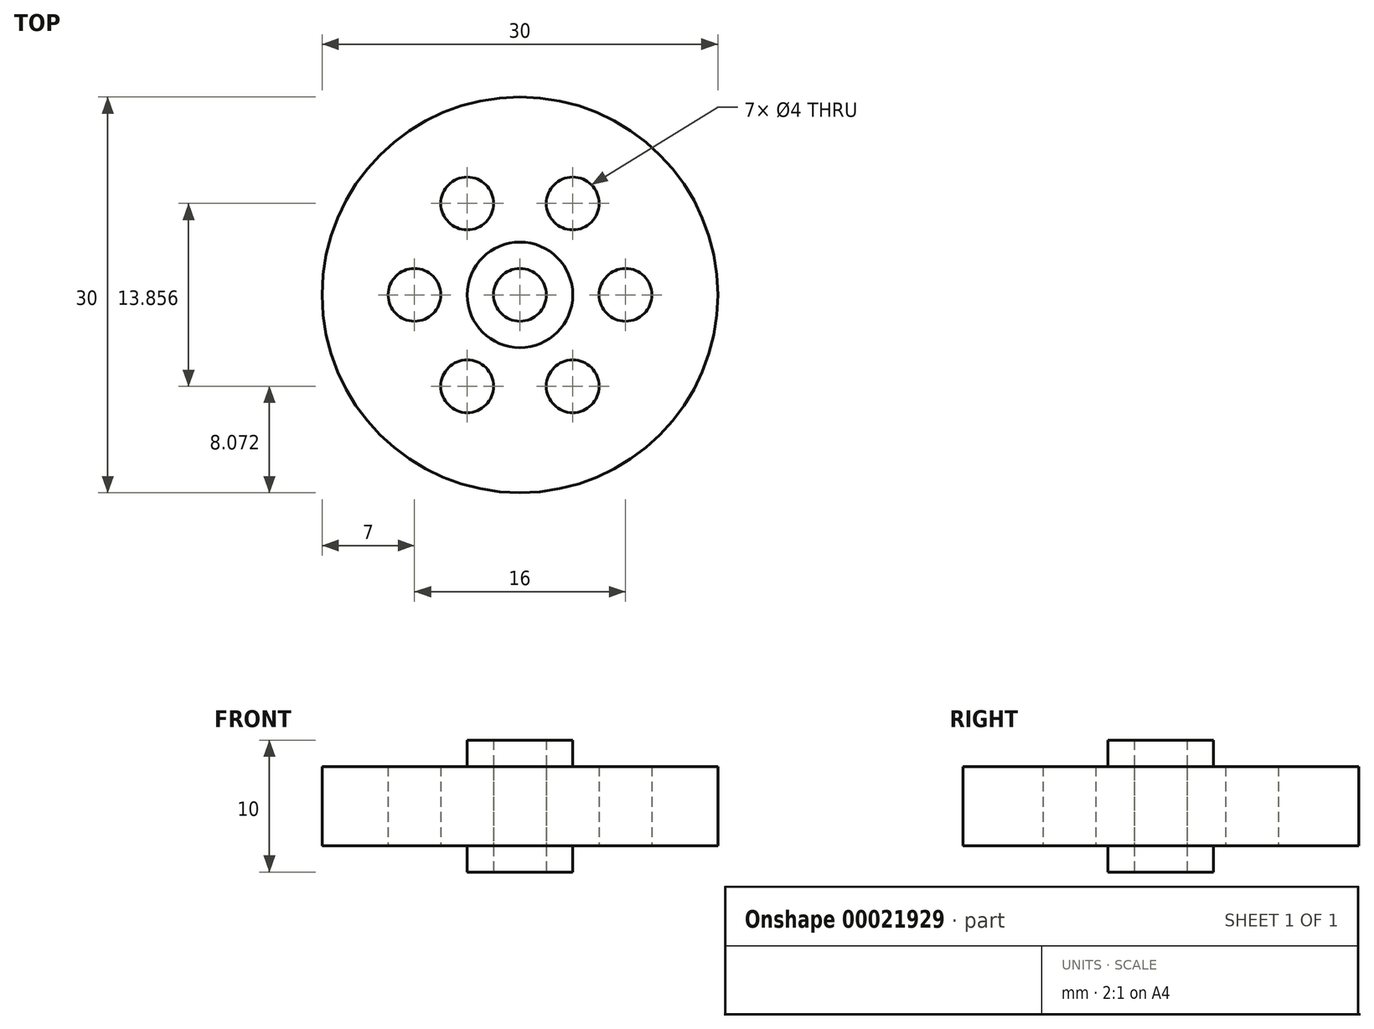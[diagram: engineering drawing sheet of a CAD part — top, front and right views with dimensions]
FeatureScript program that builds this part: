
annotation { "Feature Type Name" : "Feature", "Feature Type Description" : "" }
export const myFeature = defineFeature(function(context is Context, id is Id, definition is map)
    precondition{}
    {
        {
            var Q0;
            Q0=qCreatedBy(makeId("Top.planeOp"),FACE);
            var sketch = newSketch(context, id + "F0", { "sketchPlane" : qUnion([Q0])});
            skCircle(sketch, "E0", {"center": v(0, 0) * mm, "radius": 15 * mm});
            skCircle(sketch, "E1", {"center": v(0, 0) * mm, "radius": 2 * mm});
            skCircle(sketch, "E2", {"center": v(0, 0) * mm, "radius": 4 * mm});
            skLineSegment(sketch, "E3", {"start": v(0, 0) * mm, "end": v(6, 0) * mm});
            skCircle(sketch, "E4", {"center": v(8, 0) * mm, "radius": 2 * mm});
            skCircle(sketch, "E5.1.0", {"center": v(4, 6.93) * mm, "radius": 2 * mm});
            skCircle(sketch, "E5.2.0", {"center": v(-4, 6.93) * mm, "radius": 2 * mm});
            skCircle(sketch, "E5.3.0", {"center": v(-8, 0) * mm, "radius": 2 * mm});
            skCircle(sketch, "E5.4.0", {"center": v(-4, -6.93) * mm, "radius": 2 * mm});
            skCircle(sketch, "E5.5.0", {"center": v(4, -6.93) * mm, "radius": 2 * mm});
            skSolve(sketch);
        }
        {
            var Q0;
            Q0=makeQuery(id+"F0.imprint","IMPRINT",FACE,{"disambiguationData":[TD([[makeQuery(id+"F0.imprint","IMPRINT",EDGE,{"derivedFrom":sQuery(id+"F0.wireOp",EDGE,"E1")}),-1.0]])]});
            extrude(context, id + "F1", {"entities" : qUnion([Q0]), "endBound" : BoundingType.SYMMETRIC, "depth" : 10 * mm});
        }
        {
            var Q0;
            Q0=makeQuery(id+"F0.imprint","IMPRINT",FACE,{"disambiguationData":[TD([[makeQuery(id+"F0.imprint","IMPRINT",EDGE,{"derivedFrom":sQuery(id+"F0.wireOp",EDGE,"E0")}),1.0]])]});
            extrude(context, id + "F2", {"entities" : qUnion([Q0]), "operationType" : NewBodyOperationType.ADD, "endBound" : BoundingType.SYMMETRIC, "depth" : 6 * mm});
        }
    });
